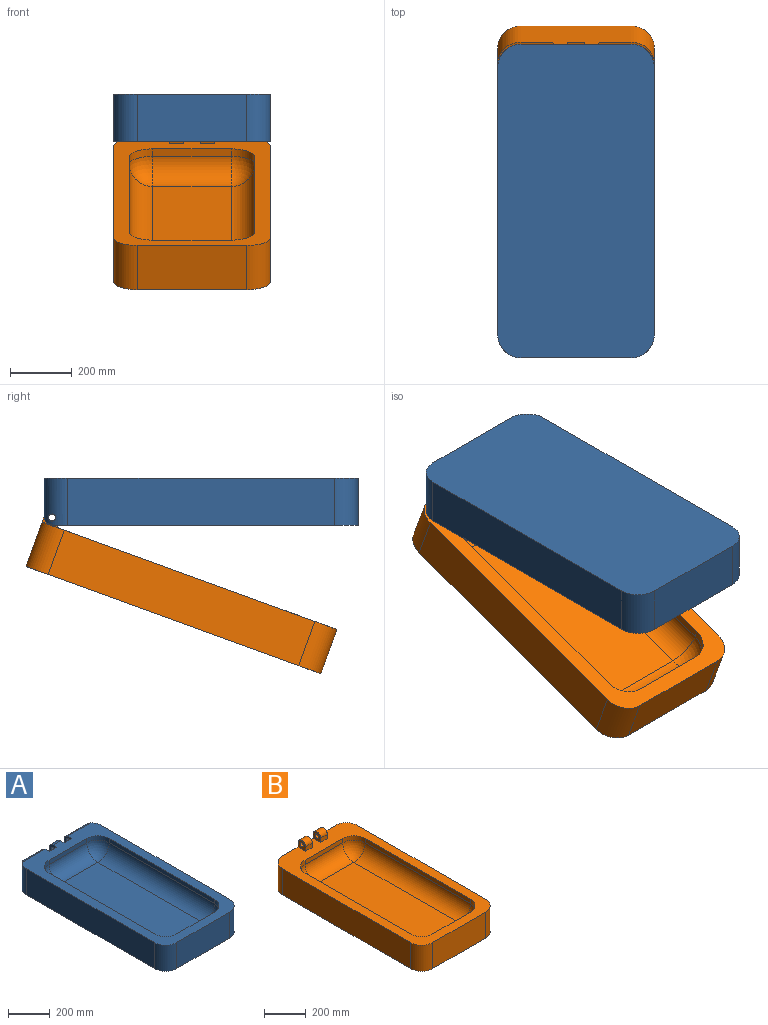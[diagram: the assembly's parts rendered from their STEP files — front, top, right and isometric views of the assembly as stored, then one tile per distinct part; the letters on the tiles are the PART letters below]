
ASSEMBLY  parts=2 mates=1
PART A: 45 faces, bbox 508x1016x152.4 mm
  f0: plane 355.6x127mm, normal (0,1,0), area 42102.6mm2, adj f1,f6,f24,f27,f29,f30,f31,f33
  f1: cylinder r=76.2mm len=152.4mm, axis (0,0,-1), area 16917.6mm2, adj f0,f2,f5,f6,f39,f42,f44
  f2: plane 993.68x508mm, normal (0,0,1), area 152517.1mm2, adj f1,f3,f4,f5,f7,f8,f9,f10
  f3: plane 863.6x152.4mm, normal (-1,0,0), area 131612.6mm2, adj f2,f6,f24,f25
  f4: plane 355.6x152.4mm, normal (0,-1,0), area 54193.4mm2, adj f2,f6,f25,f26
  f5: plane 863.6x152.4mm, normal (1,0,0), area 131612.6mm2, adj f1,f2,f6,f26
  f6: plane 1016x508mm, normal (0,0,-1), area 511143.7mm2, adj f0,f1,f3,f4,f5,f24,f25,f26
  f7: plane 254x25.4mm, normal (0,-1,0), area 6451.6mm2, adj f2,f14,f20,f23
  f8: plane 711.2x25.4mm, normal (1,0,0), area 18064.5mm2, adj f2,f17,f21,f23
  f9: plane 254x25.4mm, normal (0,1,0), area 6451.6mm2, adj f2,f12,f16,f17
  f10: plane 711.2x25.4mm, normal (-1,0,0), area 18064.5mm2, adj f2,f12,f14,f15
  f11: plane 711.2x254mm, normal (0,0,1), area 180644.8mm2, adj f15,f16,f20,f21
  f12: cylinder r=76.2mm len=76.2mm, axis (0,0,1), area 3040.2mm2, adj f2,f9,f10,f13
  f13: sphere r=76.2mm, area 9120.7mm2, adj f12,f15,f16
  f14: cylinder r=76.2mm len=76.2mm, axis (0,0,-1), area 3040.2mm2, adj f2,f7,f10,f18
  f15: cylinder r=76.2mm len=711.2mm, axis (0,1,0), area 85126.9mm2, adj f10,f11,f13,f18
  f16: cylinder r=76.2mm len=254mm, axis (1,0,0), area 30402.4mm2, adj f9,f11,f13,f19
  f17: cylinder r=76.2mm len=76.2mm, axis (0,0,-1), area 3040.2mm2, adj f2,f8,f9,f19
  f18: sphere r=76.2mm, area 9120.7mm2, adj f14,f15,f20
  f19: sphere r=76.2mm, area 9120.7mm2, adj f16,f17,f21
  f20: cylinder r=76.2mm len=254mm, axis (-1,0,0), area 30402.4mm2, adj f7,f11,f18,f22
  f21: cylinder r=76.2mm len=711.2mm, axis (0,-1,0), area 85126.9mm2, adj f8,f11,f19,f22
  f22: sphere r=76.2mm, area 9120.7mm2, adj f20,f21,f23
  f23: cylinder r=76.2mm len=76.2mm, axis (0,0,1), area 3040.2mm2, adj f2,f7,f8,f22
  f24: cylinder r=76.2mm len=152.4mm, axis (0,0,1), area 16915.9mm2, adj f0,f2,f3,f6,f38,f41,f43
  f25: cylinder r=76.2mm len=152.4mm, axis (0,0,-1), area 18241.5mm2, adj f2,f3,f4,f6
  f26: cylinder r=76.2mm len=152.4mm, axis (0,0,1), area 18241.5mm2, adj f2,f4,f5,f6
  f27: plane 50.8x50.8mm, normal (1,0,0), area 1893.3mm2, adj f0,f2,f28,f30,f35,f37,f40
  f28: plane 50.8x25.4mm, normal (0,1,0), area 1290.3mm2, adj f2,f27,f29,f35
  f29: plane 50.8x50.8mm, normal (-1,0,0), area 1841mm2, adj f0,f2,f28,f30,f35,f39,f42,f44
  f30: plane 50.8x25.4mm, normal (0,0,1), area 1290.3mm2, adj f0,f27,f29,f35
  f31: plane 50.8x50.8mm, normal (1,0,0), area 1841mm2, adj f0,f2,f32,f34,f36,f38,f41,f43
  f32: plane 50.8x25.4mm, normal (0,1,0), area 1290.3mm2, adj f2,f31,f33,f36
  f33: plane 50.8x50.8mm, normal (-1,0,0), area 1893.3mm2, adj f0,f2,f32,f34,f36,f37,f40
  f34: plane 50.8x25.4mm, normal (0,0,1), area 1290.3mm2, adj f0,f31,f33,f36
  f35: cylinder r=25.4mm len=50.8mm, axis (1,0,0), area 2026.8mm2, adj f27,f28,f29,f30
  f36: cylinder r=25.4mm len=50.8mm, axis (1,0,0), area 2026.8mm2, adj f31,f32,f33,f34
  f37: cylinder r=11.43mm len=50.8mm, axis (1,0,0), area 3648.3mm2, adj f27,f33
  f38: cylinder r=11.43mm len=166.84mm, axis (1,0,0), area 11298mm2, adj f24,f31
  f39: cylinder r=11.43mm len=166.84mm, axis (1,0,0), area 11298.2mm2, adj f1,f29
  f40: cylinder r=25.4mm len=50.8mm, axis (1,0,0), area 2026.8mm2, adj f0,f2,f27,f33
  f41: plane 155.48x2.54mm, normal (0,1,0), area 394.9mm2, adj f2,f24,f31,f43
  f42: plane 155.48x2.54mm, normal (0,1,0), area 394.9mm2, adj f1,f2,f29,f44
  f43: cylinder r=25.4mm len=155.48mm, axis (1,0,0), area 4818.5mm2, adj f0,f24,f31,f41
  f44: cylinder r=25.4mm len=155.48mm, axis (1,0,0), area 4818.5mm2, adj f0,f1,f29,f42
PART B: 37 faces, bbox 508x1016x203.2 mm
  f0: plane 1016x508mm, normal (0,0,1), area 160515.8mm2, adj f1,f2,f3,f4,f6,f7,f8,f9
  f1: plane 355.6x177.8mm, normal (0,1,0), area 56516mm2, adj f0,f5,f23,f26,f27,f29,f30,f32
  f2: plane 863.6x152.4mm, normal (-1,0,0), area 131612.6mm2, adj f0,f5,f23,f24
  f3: plane 355.6x152.4mm, normal (0,-1,0), area 54193.4mm2, adj f0,f5,f24,f25
  f4: plane 863.6x152.4mm, normal (1,0,0), area 131612.6mm2, adj f0,f5,f25,f26
  f5: plane 1016x508mm, normal (0,0,-1), area 511143.7mm2, adj f1,f2,f3,f4,f23,f24,f25,f26
  f6: plane 254x25.4mm, normal (0,-1,0), area 6451.6mm2, adj f0,f13,f19,f22
  f7: plane 711.2x25.4mm, normal (1,0,0), area 18064.5mm2, adj f0,f16,f20,f22
  f8: plane 254x25.4mm, normal (0,1,0), area 6451.6mm2, adj f0,f11,f15,f16
  f9: plane 711.2x25.4mm, normal (-1,0,0), area 18064.5mm2, adj f0,f11,f13,f14
  f10: plane 711.2x254mm, normal (0,0,1), area 180644.8mm2, adj f14,f15,f19,f20
  f11: cylinder r=76.2mm len=76.2mm, axis (0,0,1), area 3040.2mm2, adj f0,f8,f9,f12
  f12: sphere r=76.2mm, area 9120.7mm2, adj f11,f14,f15
  f13: cylinder r=76.2mm len=76.2mm, axis (0,0,-1), area 3040.2mm2, adj f0,f6,f9,f17
  f14: cylinder r=76.2mm len=711.2mm, axis (0,1,0), area 85126.9mm2, adj f9,f10,f12,f17
  f15: cylinder r=76.2mm len=254mm, axis (1,0,0), area 30402.4mm2, adj f8,f10,f12,f18
  f16: cylinder r=76.2mm len=76.2mm, axis (0,0,-1), area 3040.2mm2, adj f0,f7,f8,f18
  f17: sphere r=76.2mm, area 9120.7mm2, adj f13,f14,f19
  f18: sphere r=76.2mm, area 9120.7mm2, adj f15,f16,f20
  f19: cylinder r=76.2mm len=254mm, axis (-1,0,0), area 30402.4mm2, adj f6,f10,f17,f21
  f20: cylinder r=76.2mm len=711.2mm, axis (0,-1,0), area 85126.9mm2, adj f7,f10,f18,f21
  f21: sphere r=76.2mm, area 9120.7mm2, adj f19,f20,f22
  f22: cylinder r=76.2mm len=76.2mm, axis (0,0,1), area 3040.2mm2, adj f0,f6,f7,f21
  f23: cylinder r=76.2mm len=152.4mm, axis (0,0,1), area 18241.5mm2, adj f0,f1,f2,f5
  f24: cylinder r=76.2mm len=152.4mm, axis (0,0,-1), area 18241.5mm2, adj f0,f2,f3,f5
  f25: cylinder r=76.2mm len=152.4mm, axis (0,0,1), area 18241.5mm2, adj f0,f3,f4,f5
  f26: cylinder r=76.2mm len=152.4mm, axis (0,0,-1), area 18241.5mm2, adj f0,f1,f4,f5
  f27: plane 50.8x50.8mm, normal (-1,0,0), area 1893.3mm2, adj f0,f1,f28,f34,f36
  f28: plane 45.72x25.4mm, normal (0,-1,0), area 1161.3mm2, adj f0,f27,f29,f34
  f29: plane 50.8x50.8mm, normal (1,0,0), area 1893.3mm2, adj f0,f1,f28,f34,f36
  f30: plane 50.8x50.8mm, normal (-1,0,0), area 1893.3mm2, adj f0,f1,f31,f33,f35
  f31: plane 45.72x25.4mm, normal (0,-1,0), area 1161.3mm2, adj f0,f30,f32,f33
  f32: plane 50.8x50.8mm, normal (1,0,0), area 1893.3mm2, adj f0,f1,f31,f33,f35
  f33: cylinder r=25.4mm len=50.8mm, axis (1,0,0), area 3648.3mm2, adj f1,f30,f31,f32
  f34: cylinder r=25.4mm len=50.8mm, axis (1,0,0), area 3648.3mm2, adj f1,f27,f28,f29
  f35: cylinder r=11.43mm len=45.72mm, axis (1,0,0), area 3283.5mm2, adj f30,f32
  f36: cylinder r=11.43mm len=45.72mm, axis (1,0,0), area 3283.5mm2, adj f27,f29
PLACE A rot(axis=(0,1,0),180deg) t=(-905.2,-1.1,617.08)mm
PLACE B rot(axis=(1,0,0),20deg) t=(-502.63,103.01,77.42)mm
MATE revolute B.f33 <-> A.f35  axis (1,0,0) through (-630.25,716.95,490.08)mm
